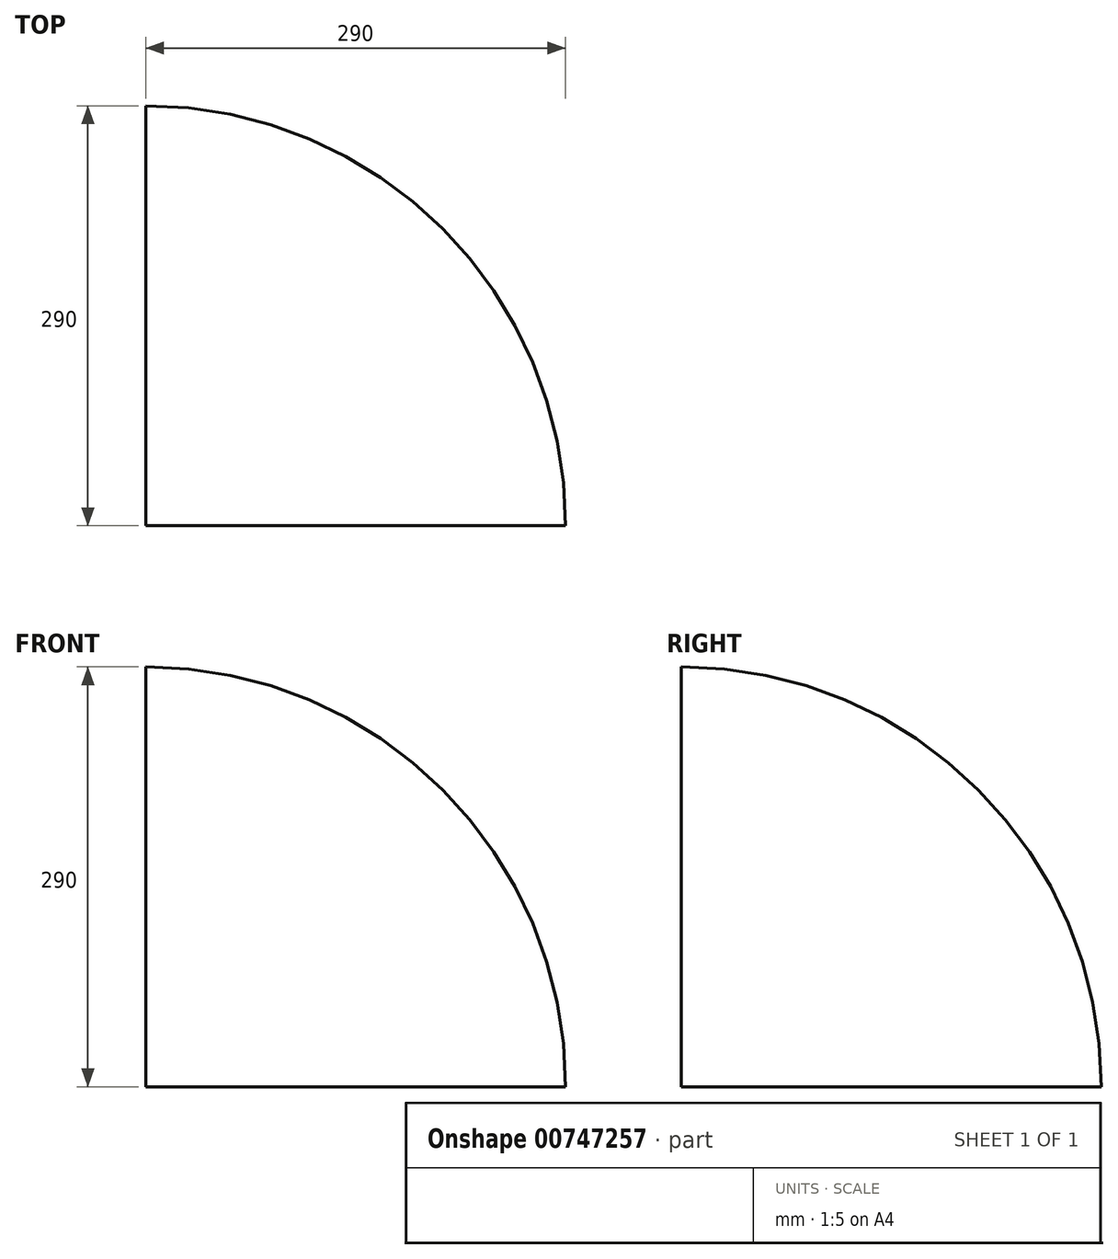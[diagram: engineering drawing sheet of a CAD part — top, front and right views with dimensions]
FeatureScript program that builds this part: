
annotation { "Feature Type Name" : "Feature", "Feature Type Description" : "" }
export const myFeature = defineFeature(function(context is Context, id is Id, definition is map)
    precondition{}
    {
        {
            var Q0;
            Q0=qCreatedBy(makeId("Top.planeOp"),FACE);
            var sketch = newSketch(context, id + "F0", { "sketchPlane" : qUnion([Q0])});
            skLineSegment(sketch, "E0.bottom", {"start": v(150, -150) * mm, "end": v(-150, -150) * mm});
            skLineSegment(sketch, "E0.top", {"start": v(150, 150) * mm, "end": v(-150, 150) * mm});
            skLineSegment(sketch, "E0.left", {"start": v(150, -150) * mm, "end": v(150, 150) * mm});
            skLineSegment(sketch, "E0.right", {"start": v(-150, -150) * mm, "end": v(-150, 150) * mm});
            skPoint(sketch, "E0.middle", {"position": v(0, 0) * mm});
            skArc(sketch, "E1", {"start": v(140, -150) * mm, "mid": v(55.06, 55.06) * mm, "end": v(-150, 140) * mm});
            skSolve(sketch);
        }
        {
            var Q0;
            {var subQ3=sQuery(id+"F0.wireOp",EDGE,"E1");Q0=makeQuery(id+"F0.imprint","IMPRINT",FACE,{"disambiguationData":[TD([[makeQuery(id+"F0.imprint","IMPRINT",EDGE,{"derivedFrom":subQ3}),1.0]])]});}
            var Q1;
            Q1=sQuery(id+"F0.wireOp",EDGE,"E0.right");
            revolve(context, id + "F1", {"surfaceOperationType" : NewSurfaceOperationType.NEW, "entities" : qUnion([Q0]), "axis" : qUnion([Q1]), "revolveType" : RevolveType.ONE_DIRECTION, "oppositeDirection" : true, "angle" : 90 * degree});
        }
    });
